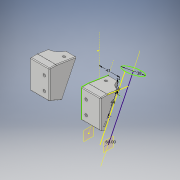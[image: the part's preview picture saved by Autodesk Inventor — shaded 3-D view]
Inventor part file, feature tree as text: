
AUTODESK INVENTOR PART (.ipt)
format: ipt  version: 2019.3 (Build 233278000, 278)  size: 339,456 bytes
history: native  units: mm
features: sketch x8, other x5, plane x4, extrude x2, hole x2, fillet x2, sweep x1, boolean_combine x1, revolve x1, mirror x1
ambient origin geometry x8: Origin, YZ Plane, XZ Plane, XY Plane, X Axis, Y Axis, Z Axis, Center Point
bodies: Body1 (feature_tree), Body2 (feature_tree), Body3 (feature_tree)
feature tree (27):
  other  "Stanchion"
  plane  "Work Plane2"
  sketch  "Sketch2"  dims[d4=0.0mm d5=0.0mm d8=10.0mm d9=0.0mm]
  plane  "Work Plane3"
  sweep  "Sweep1"
  plane  "Work Plane4"
  extrude  "Extrusion1"  Depth=28.0mm
  plane  "Work Plane5"
  hole  "Hole1"  [1 undecoded]
  sketch  "Sketch11"  dims[d36=5.25mm d37=6.0mm d38=9.3mm d39=4.0mm d40=90.0deg d41=20.5mm d42=0.0mm]
  extrude  "Extrusion2"  Depth=2.5mm
  fillet  "Fillet4"  Radius=8.5mm
  boolean_combine  "Combine1"
  other  "Work Axis3"
  revolve  "Revolution1"  [1 undecoded]
  fillet  "Fillet3"  Radius=2.5mm
  hole  "Hole2"  [1 undecoded]
  mirror  "Mirror3"
  sketch  "Sketch3"  dims[d10=-69.25mm d11=28.0mm]
  sketch  "Sketch4"  dims[d12=5.5mm d13=6.0mm d14=9.3mm d15=54.75mm d16=90.0deg d17=8.0mm d18=20.594885mm d27=8.5mm]
  sketch  "Sketch6"  dims[d28=2.7mm d29=2.5mm d30=8.5mm]
  other  "Marzocchi-380-FixRight"
  sketch  "Sketch9"  dims[d31=90.0deg d32=1.5mm d33=2.5mm]
  other  "Pattern of Marzocchi-380-FixRight:2"
  other  "Marzocchi-380-FixLeft"
  sketch  "Sketch10"  dims[d34=2.7mm d35=14.0mm]
  sketch  "Sketch12"  dims[d43=44.0mm d44=36.25mm d45=10.0mm d46=0.0mm d47=1.75mm d48=0.375mm d49=14.3117mm d50=0.75mm d51=20.594885mm d52=0.0625mm d53=0.75mm d54=0.375mm]
note: 3 required parameter values undecoded (feature->parameter linkage not recoverable at this tier; creation-order binding heuristic only, values carry confidence <= 0.55)